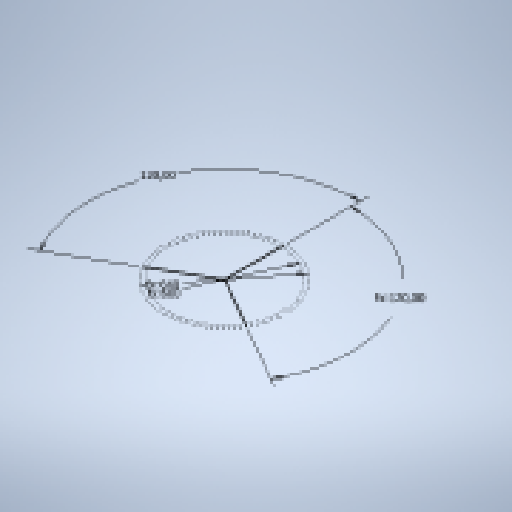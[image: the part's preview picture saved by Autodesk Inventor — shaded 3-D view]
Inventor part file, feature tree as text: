
AUTODESK INVENTOR PART (.ipt)
format: ipt  version: 2025 (Build 290162010, 162A)  size: 135,680 bytes
history: native  units: mm
features: sketch x1
ambient origin geometry x8: Origin, YZ Plane, XZ Plane, XY Plane, X Axis, Y Axis, Z Axis, Center Point
feature tree (1):
  sketch  "Sketch1"  dims[d1=600.0mm d2=120.0deg d3=120.0deg d4=640.0mm]
